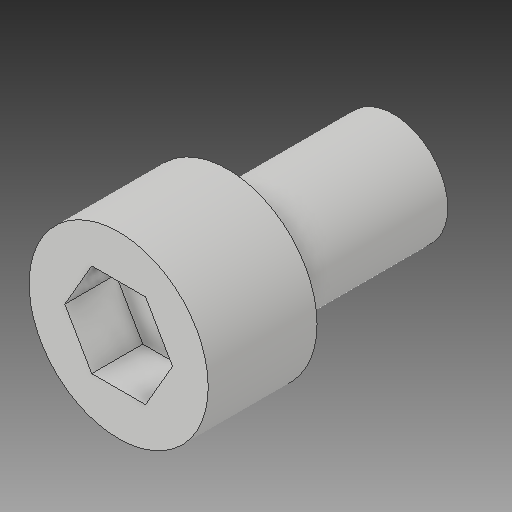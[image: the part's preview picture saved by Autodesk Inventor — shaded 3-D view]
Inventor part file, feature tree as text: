
AUTODESK INVENTOR PART (.ipt)
format: ipt  version: 2017 (Build 210142000, 142)  size: 130,560 bytes
history: native  units: in
note: dims shown in document units (in); Inventor stores cm internally (conversion verified against a paired STEP export)
features: other x13, extrude x3, sketch x3
ambient origin geometry x8: Origin, YZ Plane, XZ Plane, XY Plane, X Axis, Y Axis, Z Axis, Center Point
bodies: Solid1 (feature_tree)
feature tree (19):
  other  "Table"
  other  "shcs-8-0250"
  other  "shcs-8-0500"
  other  "shcs-8-0750"
  other  "shcs-8-1000"
  other  "shcs-8-1250"
  other  "shcs-8-1500"
  other  "shcs-8-1750"
  other  "shcs-8-2000"
  other  "shcs-8-2250"
  other  "shcs-8-2500"
  other  "shcs-8-2750"
  other  "shcs-8-3000"
  extrude  "Extrusion1"  TaperAngle=0.0deg  [1 undecoded]
  extrude  "Extrusion2"  [1 undecoded]
  extrude  "Extrusion3"  [1 undecoded]
  sketch  "Sketch1"  dims[d1=0.0in d4=0.0in]
  sketch  "Sketch2"  dims[d7=0.0in]
  sketch  "Sketch3"
note: 3 required parameter values undecoded (feature->parameter linkage not recoverable at this tier; creation-order binding heuristic only, values carry confidence <= 0.55)
